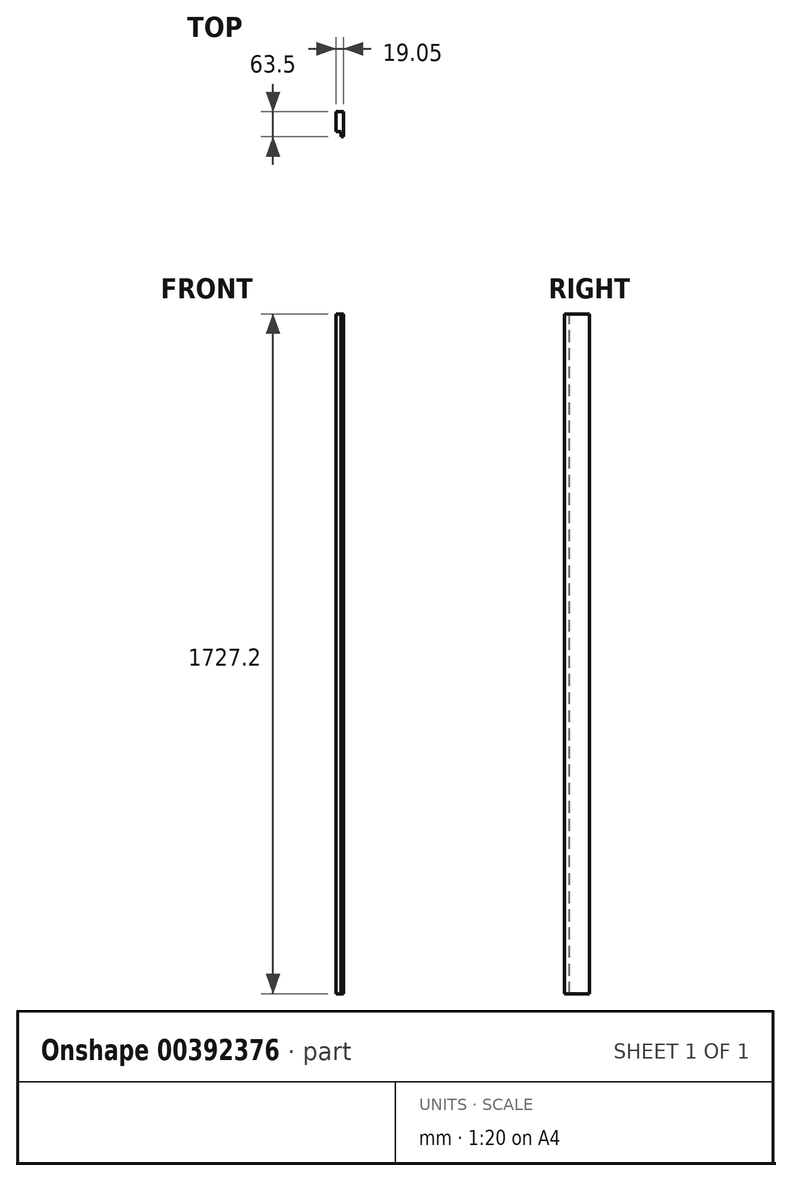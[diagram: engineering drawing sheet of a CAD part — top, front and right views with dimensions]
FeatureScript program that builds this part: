
annotation { "Feature Type Name" : "Feature", "Feature Type Description" : "" }
export const myFeature = defineFeature(function(context is Context, id is Id, definition is map)
    precondition{}
    {
        {
            var Q0;
            Q0=qCreatedBy(makeId("Top.planeOp"),FACE);
            var sketch = newSketch(context, id + "F0", { "sketchPlane" : qUnion([Q0])});
            skLineSegment(sketch, "E0.bottom", {"start": v(142.78, 0) * mm, "end": v(161.83, 0) * mm});
            skLineSegment(sketch, "E0.top", {"start": v(142.78, -63.5) * mm, "end": v(161.83, -63.5) * mm});
            skLineSegment(sketch, "E0.left", {"start": v(142.78, 0) * mm, "end": v(142.78, -63.5) * mm});
            skLineSegment(sketch, "E0.right", {"start": v(161.83, 0) * mm, "end": v(161.83, -63.5) * mm});
            skSolve(sketch);
        }
        {
            var Q0;
            Q0=qSketchRegion(id+"F0",true);
            extrude(context, id + "F1", {"entities" : qUnion([Q0]), "depth" : 1727.2 * mm});
        }
        {
            var Q0;
            Q0=makeQuery(id+"F1.opExtrude","CAP_FACE",FACE,{"disambiguationData":[OSD([sQuery(id+"F0.wireOp",EDGE,"E0.bottom"),sQuery(id+"F0.wireOp",EDGE,"E0.top"),sQuery(id+"F0.wireOp",EDGE,"E0.left"),sQuery(id+"F0.wireOp",EDGE,"E0.right")])],"isStart":false});
            var sketch = newSketch(context, id + "F2", { "sketchPlane" : qUnion([Q0])});
            skLineSegment(sketch, "E1", {"start": v(155.48, -63.5) * mm, "end": v(155.48, -50.8) * mm});
            skLineSegment(sketch, "E2", {"start": v(155.48, -50.8) * mm, "end": v(142.78, -50.8) * mm});
            skSolve(sketch);
        }
        {
            var Q0;
            Q0=qSketchRegion(id+"F2",true);
            var Q1;
            {var subQ0=sQuery(id+"F2.wireOp",EDGE,"E1");Q1=makeQuery(id+"F2.imprint","IMPRINT",FACE,{"disambiguationData":[TD([[makeQuery(id+"F2.imprint","IMPRINT",EDGE,{"derivedFrom":subQ0}),1.0]])]});}
            extrude(context, id + "F3", {"entities" : qUnion([Q0, Q1]), "operationType" : NewBodyOperationType.REMOVE, "endBound" : BoundingType.THROUGH_ALL, "oppositeDirection" : true, "depth" : 25.4 * mm});
        }
    });
